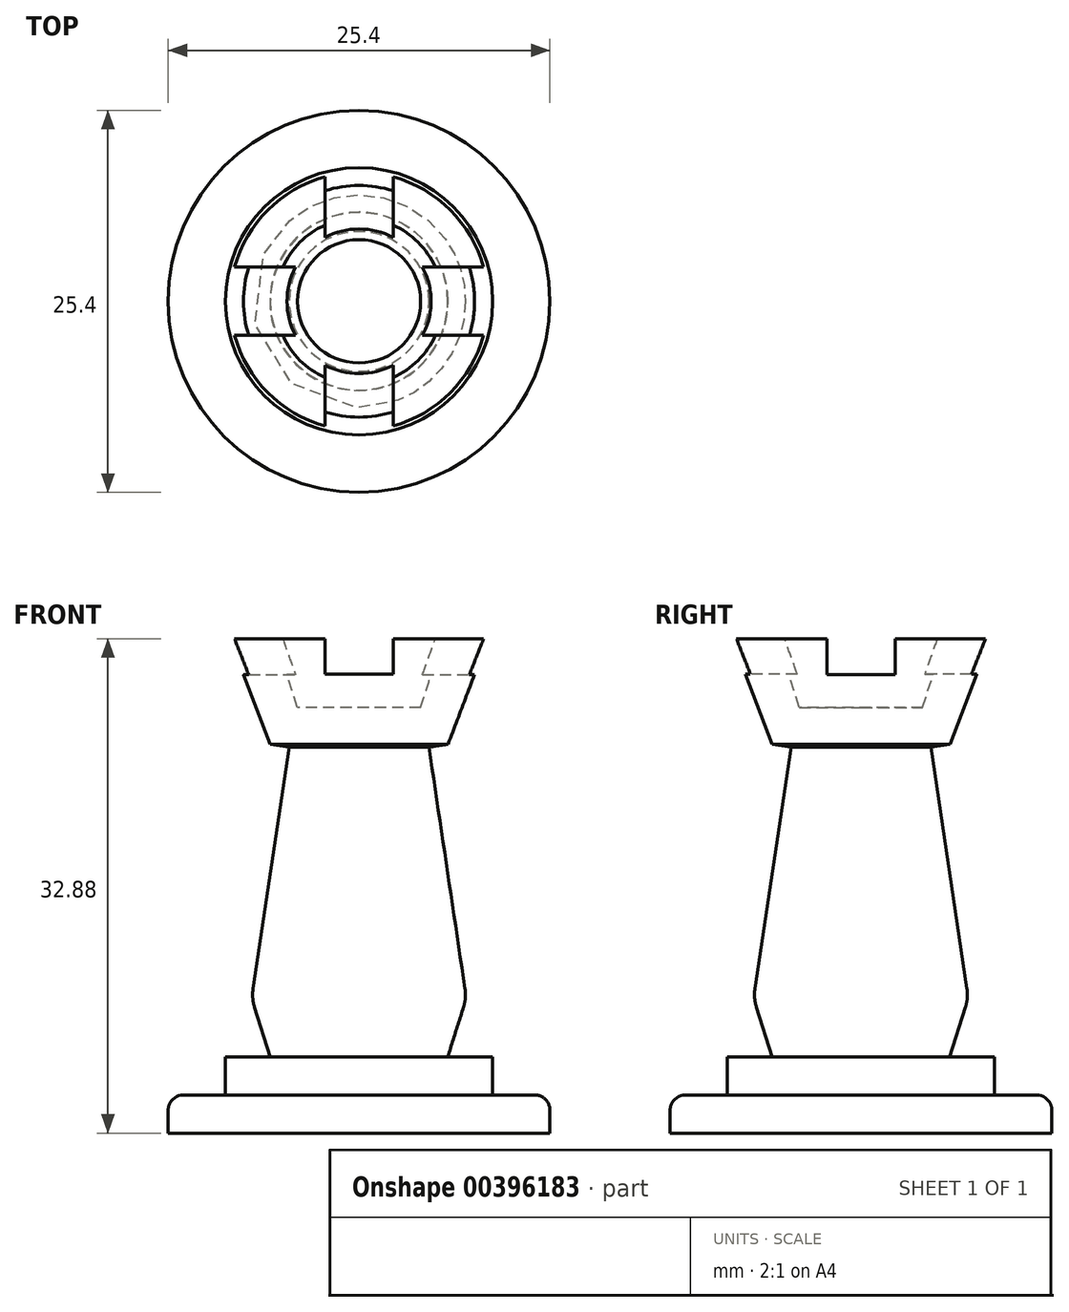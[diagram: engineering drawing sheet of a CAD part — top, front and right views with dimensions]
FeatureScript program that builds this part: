
annotation { "Feature Type Name" : "Feature", "Feature Type Description" : "" }
export const myFeature = defineFeature(function(context is Context, id is Id, definition is map)
    precondition{}
    {
        {
            var Q0;
            Q0=qCreatedBy(makeId("Top.planeOp"),FACE);
            var sketch = newSketch(context, id + "F0", { "sketchPlane" : qUnion([Q0])});
            skCircle(sketch, "E0", {"center": v(0, 0) * mm, "radius": 12.7 * mm});
            skCircle(sketch, "E1", {"center": v(0, 0) * mm, "radius": 8.9 * mm});
            skCircle(sketch, "E2", {"center": v(0, 0) * mm, "radius": 6.35 * mm});
            skCircle(sketch, "E3", {"center": v(0, 0) * mm, "radius": 3.81 * mm});
            skSolve(sketch);
        }
        {
            var Q0;
            Q0=makeQuery(id+"F0.imprint","IMPRINT",FACE,{"disambiguationData":[TD([[makeQuery(id+"F0.imprint","IMPRINT",EDGE,{"derivedFrom":sQuery(id+"F0.wireOp",EDGE,"E2")}),1.0]])]});
            var Q1;
            Q1=makeQuery(id+"F0.imprint","IMPRINT",FACE,{"disambiguationData":[TD([[makeQuery(id+"F0.imprint","IMPRINT",EDGE,{"derivedFrom":sQuery(id+"F0.wireOp",EDGE,"E1")}),1.0]])]});
            var Q2;
            Q2=makeQuery(id+"F0.imprint","IMPRINT",FACE,{"disambiguationData":[TD([[makeQuery(id+"F0.imprint","IMPRINT",EDGE,{"derivedFrom":sQuery(id+"F0.wireOp",EDGE,"E0")}),1.0]])]});
            var Q3;
            Q3=makeQuery(id+"F0.imprint","IMPRINT",FACE,{"disambiguationData":[TD([[makeQuery(id+"F0.imprint","IMPRINT",EDGE,{"derivedFrom":sQuery(id+"F0.wireOp",EDGE,"E3")}),1.0]])]});
            extrude(context, id + "F1", {"entities" : qUnion([Q0, Q1, Q2, Q3]), "oppositeDirection" : true, "depth" : 2.54 * mm});
        }
        {
            var Q0;
            Q0=makeQuery(id+"F0.imprint","IMPRINT",FACE,{"disambiguationData":[TD([[makeQuery(id+"F0.imprint","IMPRINT",EDGE,{"derivedFrom":sQuery(id+"F0.wireOp",EDGE,"E1")}),1.0]])]});
            var Q1;
            Q1=makeQuery(id+"F0.imprint","IMPRINT",FACE,{"disambiguationData":[TD([[makeQuery(id+"F0.imprint","IMPRINT",EDGE,{"derivedFrom":sQuery(id+"F0.wireOp",EDGE,"E2")}),1.0]])]});
            var Q2;
            Q2=makeQuery(id+"F0.imprint","IMPRINT",FACE,{"disambiguationData":[TD([[makeQuery(id+"F0.imprint","IMPRINT",EDGE,{"derivedFrom":sQuery(id+"F0.wireOp",EDGE,"E3")}),1.0]])]});
            extrude(context, id + "F2", {"entities" : qUnion([Q0, Q1, Q2]), "operationType" : NewBodyOperationType.ADD, "depth" : 2.54 * mm});
        }
        {
            var Q0;
            Q0=makeQuery(id+"F2.opExtrude","CAP_EDGE",EDGE,{"disambiguationData":[OSD([sQuery(id+"F0.wireOp",EDGE,"E1")])],"isStart":true});
            var Q1;
            Q1=makeQuery(id+"F1.opExtrude","CAP_EDGE",EDGE,{"disambiguationData":[OSD([sQuery(id+"F0.wireOp",EDGE,"E0")])],"isStart":true});
            fillet(context, id + "F3", {"entities" : qUnion([Q0, Q1]), "radius" : 1.02 * mm, "tangentPropagation" : true, "allowEdgeOverflow" : false});
        }
        {
            var Q0;
            Q0=qCreatedBy(makeId("Right.planeOp"),FACE);
            var sketch = newSketch(context, id + "F4", { "sketchPlane" : qUnion([Q0])});
            skLineSegment(sketch, "E4", {"start": v(-6.95, 5.84) * mm, "end": v(-5.85, 2.37) * mm});
            skLineSegment(sketch, "E5", {"start": v(-5.85, 2.37) * mm, "end": v(0, 2.37) * mm});
            skLineSegment(sketch, "E6", {"start": v(0, 2.37) * mm, "end": v(0, 24.71) * mm});
            skLineSegment(sketch, "E7", {"start": v(0, 24.71) * mm, "end": v(0, 2.37) * mm});
            skPoint(sketch, "E8.visualSharp", {"position": v(-7.15, 6.45) * mm});
            skArc(sketch, "E8.filletArc", {"start": v(-7.05, 7.07) * mm, "mid": v(-7.07, 6.45) * mm, "end": v(-6.95, 5.84) * mm});
            skLineSegment(sketch, "E9.trimOffspring", {"start": v(-4.65, 23.14) * mm, "end": v(-7.05, 7.07) * mm});
            skPoint(sketch, "E10.start.orphan", {"position": v(0, 28) * mm});
            skLineSegment(sketch, "E11", {"start": v(0, 23.57) * mm, "end": v(0, 24.81) * mm});
            skLineSegment(sketch, "E12", {"start": v(-4.65, 23.14) * mm, "end": v(-5.93, 23.33) * mm});
            skLineSegment(sketch, "E13", {"start": v(-5.93, 23.33) * mm, "end": v(-7.84, 28.36) * mm});
            skLineSegment(sketch, "E14", {"start": v(-4.93, 28.36) * mm, "end": v(-4.1, 25.78) * mm});
            skLineSegment(sketch, "E15", {"start": v(-4.1, 25.78) * mm, "end": v(0, 25.78) * mm});
            skLineSegment(sketch, "E16", {"start": v(0, 25.78) * mm, "end": v(0, 21.91) * mm});
            skLineSegment(sketch, "E17", {"start": v(-4.1, 25.78) * mm, "end": v(-5.56, 30.34) * mm});
            skLineSegment(sketch, "E18", {"start": v(-5.93, 23.33) * mm, "end": v(-8.6, 30.34) * mm});
            skLineSegment(sketch, "E19", {"start": v(-8.6, 30.34) * mm, "end": v(-5.64, 30.34) * mm});
            skLineSegment(sketch, "E20", {"start": v(-5.64, 30.34) * mm, "end": v(-5.56, 30.34) * mm});
            skPoint(sketch, "E21.orphan", {"position": v(-5.64, 30.61) * mm});
            skSolve(sketch);
        }
        {
            var Q0;
            Q0=makeQuery(id+"F4.imprint","IMPRINT",FACE,{"disambiguationData":[TD([[makeQuery(id+"F4.imprint","IMPRINT",EDGE,{"derivedFrom":sQuery(id+"F4.wireOp",EDGE,"E4")}),1.0]])]});
            var Q1;
            Q1=sQuery(id+"F4.wireOp",EDGE,"E7");
            revolve(context, id + "F5", {"operationType" : NewBodyOperationType.ADD, "entities" : qUnion([Q0]), "axis" : qUnion([Q1]), "revolveType" : RevolveType.FULL});
        }
        {
            var Q0;
            Q0=qCreatedBy(makeId("Front.planeOp"),FACE);
            var sketch = newSketch(context, id + "F6", { "sketchPlane" : qUnion([Q0])});
            skLineSegment(sketch, "E22", {"start": v(0, 28) * mm, "end": v(-2.27, 28) * mm});
            skLineSegment(sketch, "E23", {"start": v(-2.27, 28) * mm, "end": v(-2.27, 30.47) * mm});
            skLineSegment(sketch, "E24", {"start": v(-2.27, 30.47) * mm, "end": v(0, 30.47) * mm});
            skLineSegment(sketch, "E25.MirrorCS", {"start": v(2.27, 30.47) * mm, "end": v(0, 30.47) * mm});
            skLineSegment(sketch, "E26.MirrorCS", {"start": v(2.27, 28) * mm, "end": v(2.27, 30.47) * mm});
            skLineSegment(sketch, "E27.MirrorCS", {"start": v(0, 28) * mm, "end": v(2.27, 28) * mm});
            skSolve(sketch);
        }
        {
            var Q0;
            Q0 = qSketchRegion(id + "F6", true);
            extrude(context, id + "F7", {"entities" : qUnion([Q0]), "operationType" : NewBodyOperationType.REMOVE, "oppositeDirection" : true, "depth" : 25.4 * mm, "hasSecondDirection" : true, "secondDirectionOppositeDirection" : false, "secondDirectionDepth" : 25.4 * mm});
        }
        {
            var Q0;
            Q0=qCreatedBy(makeId("Right.planeOp"),FACE);
            var sketch = newSketch(context, id + "F8", { "sketchPlane" : qUnion([Q0])});
            skLineSegment(sketch, "E28", {"start": v(0, 27.96) * mm, "end": v(-2.27, 27.96) * mm});
            skLineSegment(sketch, "E29", {"start": v(-2.27, 27.96) * mm, "end": v(-2.27, 31.45) * mm});
            skLineSegment(sketch, "E30", {"start": v(-2.27, 31.45) * mm, "end": v(0, 31.45) * mm});
            skLineSegment(sketch, "E31.MirrorCS", {"start": v(2.27, 31.45) * mm, "end": v(0, 31.45) * mm});
            skLineSegment(sketch, "E32.MirrorCS", {"start": v(2.27, 27.96) * mm, "end": v(2.27, 31.45) * mm});
            skLineSegment(sketch, "E33.MirrorCS", {"start": v(0, 27.96) * mm, "end": v(2.27, 27.96) * mm});
            skSolve(sketch);
        }
        {
            var Q0;
            Q0 = qSketchRegion(id + "F8", true);
            extrude(context, id + "F9", {"entities" : qUnion([Q0]), "operationType" : NewBodyOperationType.REMOVE, "oppositeDirection" : true, "depth" : 25.4 * mm, "hasSecondDirection" : true, "secondDirectionOppositeDirection" : false, "secondDirectionDepth" : 25.4 * mm});
        }
    });
